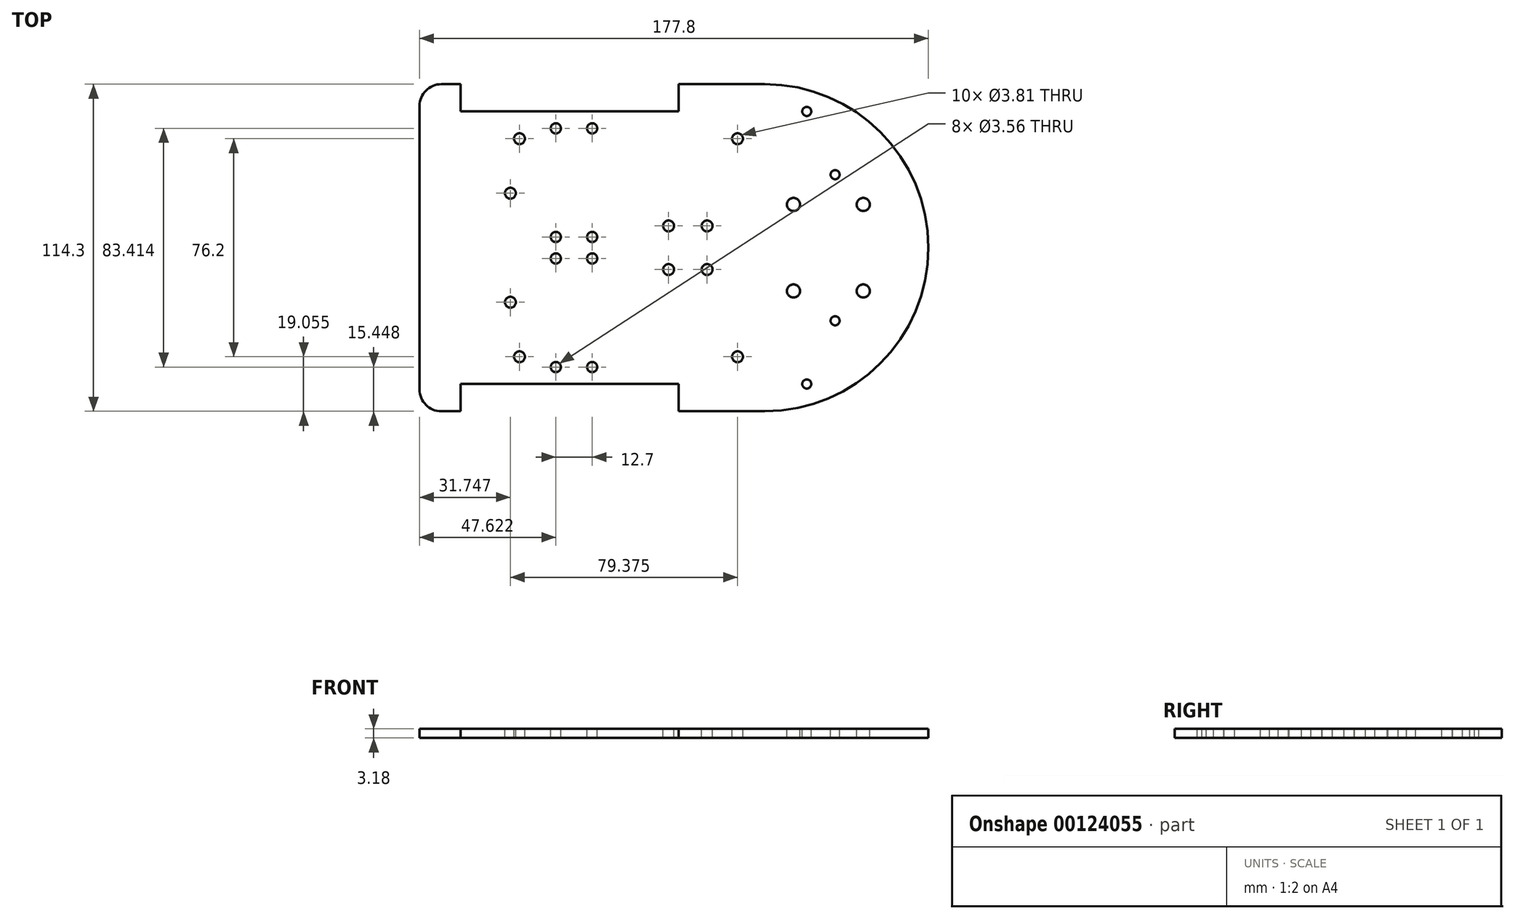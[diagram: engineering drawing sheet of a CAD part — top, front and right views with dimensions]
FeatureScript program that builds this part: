
annotation { "Feature Type Name" : "Feature", "Feature Type Description" : "" }
export const myFeature = defineFeature(function(context is Context, id is Id, definition is map)
    precondition{}
    {
        {
            var Q0;
            Q0=qCreatedBy(makeId("Top.planeOp"),FACE);
            var sketch = newSketch(context, id + "F0", { "sketchPlane" : qUnion([Q0])});
            skLineSegment(sketch, "E0.bottom", {"start": v(-54.24, -6.62) * mm, "end": v(123.56, -6.62) * mm});
            skLineSegment(sketch, "E0.top", {"start": v(-54.24, 107.68) * mm, "end": v(123.56, 107.68) * mm});
            skLineSegment(sketch, "E0.left", {"start": v(-54.24, -6.62) * mm, "end": v(-54.24, 107.68) * mm});
            skLineSegment(sketch, "E0.right", {"start": v(123.56, -6.62) * mm, "end": v(123.56, 107.68) * mm});
            skSolve(sketch);
        }
        {
            var Q0;
            Q0=makeQuery(id+"F0.imprint","IMPRINT",FACE,{"disambiguationData":[TD([[makeQuery(id+"F0.imprint","IMPRINT",EDGE,{"derivedFrom":sQuery(id+"F0.wireOp",EDGE,"E0.bottom")}),1.0]])]});
            extrude(context, id + "F1", {"entities" : qUnion([Q0]), "depth" : 3.17 * mm});
        }
        {
            var Q0;
            Q0=makeQuery(id+"F1.opExtrude","SWEPT_EDGE",EDGE,{"disambiguationData":[OSD([sQuery(id+"F0.wireOp",EDGE,"E0.top"),sQuery(id+"F0.wireOp",EDGE,"E0.left")])]});
            var Q1;
            Q1=makeQuery(id+"F1.opExtrude","SWEPT_EDGE",EDGE,{"disambiguationData":[OSD([sQuery(id+"F0.wireOp",EDGE,"E0.bottom"),sQuery(id+"F0.wireOp",EDGE,"E0.left")])]});
            fillet(context, id + "F2", {"entities" : qUnion([Q0, Q1]), "radius" : 7.62 * mm, "tangentPropagation" : true, "allowEdgeOverflow" : false});
        }
        {
            var Q0;
            Q0=makeQuery(id+"F1.opExtrude","CAP_FACE",FACE,{"disambiguationData":[OSD([sQuery(id+"F0.wireOp",EDGE,"E0.bottom"),sQuery(id+"F0.wireOp",EDGE,"E0.top"),sQuery(id+"F0.wireOp",EDGE,"E0.left"),sQuery(id+"F0.wireOp",EDGE,"E0.right")])],"isStart":false});
            var sketch = newSketch(context, id + "F3", { "sketchPlane" : qUnion([Q0])});
            skLineSegment(sketch, "E1.bottom", {"start": v(-39.96, -6.62) * mm, "end": v(36.24, -6.62) * mm});
            skLineSegment(sketch, "E1.top", {"start": v(-39.96, 2.9) * mm, "end": v(36.24, 2.9) * mm});
            skLineSegment(sketch, "E1.left", {"start": v(-39.96, -6.62) * mm, "end": v(-39.96, 2.9) * mm});
            skLineSegment(sketch, "E1.right", {"start": v(36.24, -6.62) * mm, "end": v(36.24, 2.9) * mm});
            skLineSegment(sketch, "E2.bottom", {"start": v(-39.96, 98.16) * mm, "end": v(36.24, 98.16) * mm});
            skLineSegment(sketch, "E2.top", {"start": v(-39.96, 107.68) * mm, "end": v(36.24, 107.68) * mm});
            skLineSegment(sketch, "E2.left", {"start": v(-39.96, 98.16) * mm, "end": v(-39.96, 107.68) * mm});
            skLineSegment(sketch, "E2.right", {"start": v(36.24, 98.16) * mm, "end": v(36.24, 107.68) * mm});
            skSolve(sketch);
        }
        {
            var Q0;
            Q0=makeQuery(id+"F3.imprint","IMPRINT",FACE,{"disambiguationData":[TD([[makeQuery(id+"F3.imprint","IMPRINT",EDGE,{"derivedFrom":sQuery(id+"F3.wireOp",EDGE,"E1.bottom")}),1.0]])]});
            var Q1;
            Q1=makeQuery(id+"F3.imprint","IMPRINT",FACE,{"disambiguationData":[TD([[makeQuery(id+"F3.imprint","IMPRINT",EDGE,{"derivedFrom":sQuery(id+"F3.wireOp",EDGE,"E2.bottom")}),1.0]])]});
            extrude(context, id + "F4", {"entities" : qUnion([Q0, Q1]), "operationType" : NewBodyOperationType.REMOVE, "oppositeDirection" : true, "depth" : 25.4 * mm});
        }
        {
            var Q0;
            Q0=makeQuery(id+"F1.opExtrude","CAP_FACE",FACE,{"disambiguationData":[OSD([sQuery(id+"F0.wireOp",EDGE,"E0.bottom"),sQuery(id+"F0.wireOp",EDGE,"E0.top"),sQuery(id+"F0.wireOp",EDGE,"E0.left"),sQuery(id+"F0.wireOp",EDGE,"E0.right")])],"isStart":false});
            var sketch = newSketch(context, id + "F5", { "sketchPlane" : qUnion([Q0])});
            skPoint(sketch, "E3", {"position": v(-6.62, 8.83) * mm});
            skPoint(sketch, "E4", {"position": v(-6.62, 46.78) * mm});
            skPoint(sketch, "E5", {"position": v(-6.62, 54.3) * mm});
            skPoint(sketch, "E6", {"position": v(-6.62, 92.24) * mm});
            skPoint(sketch, "E7", {"position": v(6.08, 8.83) * mm});
            skPoint(sketch, "E8", {"position": v(6.08, 46.78) * mm});
            skPoint(sketch, "E9", {"position": v(6.08, 54.3) * mm});
            skPoint(sketch, "E10", {"position": v(6.08, 92.24) * mm});
            skSolve(sketch);
        }
        {
            var Q0;
            Q0=sQuery(id+"F5.wireOp",VERTEX,"E3");
            var Q1;
            Q1=sQuery(id+"F5.wireOp",VERTEX,"E4");
            var Q2;
            Q2=sQuery(id+"F5.wireOp",VERTEX,"E5");
            var Q3;
            Q3=sQuery(id+"F5.wireOp",VERTEX,"E6");
            var Q4;
            Q4=sQuery(id+"F5.wireOp",VERTEX,"E7");
            var Q5;
            Q5=sQuery(id+"F5.wireOp",VERTEX,"E8");
            var Q6;
            Q6=sQuery(id+"F5.wireOp",VERTEX,"E9");
            var Q7;
            Q7=sQuery(id+"F5.wireOp",VERTEX,"E10");
            var Q8;
            Q8=makeQuery(id+"F1.opExtrude","SWEPT_BODY",BODY,{"disambiguationData":[OSD([sQuery(id+"F0.wireOp",EDGE,"E0.bottom"),sQuery(id+"F0.wireOp",EDGE,"E0.top"),sQuery(id+"F0.wireOp",EDGE,"E0.left"),sQuery(id+"F0.wireOp",EDGE,"E0.right")])]});
            hole(context, id + "F6", {"style" : HoleStyle.SIMPLE, "endStyle" : HoleEndStyle.THROUGH, "holeDiameter" : 3.56 * mm, "locations" : qUnion([Q0, Q1, Q2, Q3, Q4, Q5, Q6, Q7]), "scope" : qUnion([Q8]), "isTappedThrough" : true});
        }
        {
            var Q0;
            Q0=makeQuery(id+"F1.opExtrude","CAP_FACE",FACE,{"disambiguationData":[OSD([sQuery(id+"F0.wireOp",EDGE,"E0.bottom"),sQuery(id+"F0.wireOp",EDGE,"E0.top"),sQuery(id+"F0.wireOp",EDGE,"E0.left"),sQuery(id+"F0.wireOp",EDGE,"E0.right")])],"isStart":false});
            var sketch = newSketch(context, id + "F7", { "sketchPlane" : qUnion([Q0])});
            skPoint(sketch, "E11", {"position": v(32.78, 58.15) * mm});
            skPoint(sketch, "E12", {"position": v(32.78, 42.91) * mm});
            skPoint(sketch, "E13", {"position": v(46.24, 42.91) * mm});
            skPoint(sketch, "E14", {"position": v(46.24, 58.15) * mm});
            skSolve(sketch);
        }
        {
            var Q0;
            Q0=sQuery(id+"F7.wireOp",VERTEX,"E12");
            var Q1;
            Q1=sQuery(id+"F7.wireOp",VERTEX,"E13");
            var Q2;
            Q2=sQuery(id+"F7.wireOp",VERTEX,"E14");
            var Q3;
            Q3=sQuery(id+"F7.wireOp",VERTEX,"E11");
            var Q4;
            Q4=makeQuery(id+"F1.opExtrude","SWEPT_BODY",BODY,{"disambiguationData":[OSD([sQuery(id+"F0.wireOp",EDGE,"E0.bottom"),sQuery(id+"F0.wireOp",EDGE,"E0.top"),sQuery(id+"F0.wireOp",EDGE,"E0.left"),sQuery(id+"F0.wireOp",EDGE,"E0.right")])]});
            hole(context, id + "F8", {"style" : HoleStyle.SIMPLE, "endStyle" : HoleEndStyle.THROUGH, "holeDiameter" : 3.8 * mm, "locations" : qUnion([Q0, Q1, Q2, Q3]), "scope" : qUnion([Q4]), "isTappedThrough" : true});
        }
        {
            var Q0;
            Q0=makeQuery(id+"F1.opExtrude","CAP_FACE",FACE,{"disambiguationData":[OSD([sQuery(id+"F0.wireOp",EDGE,"E0.bottom"),sQuery(id+"F0.wireOp",EDGE,"E0.top"),sQuery(id+"F0.wireOp",EDGE,"E0.left"),sQuery(id+"F0.wireOp",EDGE,"E0.right")])],"isStart":false});
            var sketch = newSketch(context, id + "F9", { "sketchPlane" : qUnion([Q0])});
            skPoint(sketch, "E15", {"position": v(46.85, 26.53) * mm});
            skPoint(sketch, "E16", {"position": v(46.85, 74.54) * mm});
            skPoint(sketch, "E17", {"position": v(97.62, 59.68) * mm});
            skPoint(sketch, "E18", {"position": v(97.62, 31.74) * mm});
            skSolve(sketch);
        }
        {
            var Q0;
            Q0=makeQuery(id+"F1.opExtrude","CAP_FACE",FACE,{"disambiguationData":[OSD([sQuery(id+"F0.wireOp",EDGE,"E0.bottom"),sQuery(id+"F0.wireOp",EDGE,"E0.top"),sQuery(id+"F0.wireOp",EDGE,"E0.left"),sQuery(id+"F0.wireOp",EDGE,"E0.right")])],"isStart":false});
            var sketch = newSketch(context, id + "F10", { "sketchPlane" : qUnion([Q0])});
            skPoint(sketch, "E19", {"position": v(-22.5, 69.58) * mm});
            skPoint(sketch, "E20", {"position": v(-22.5, 31.48) * mm});
            skSolve(sketch);
        }
        {
            var Q0;
            Q0=sQuery(id+"F10.wireOp",VERTEX,"E20");
            var Q1;
            Q1=sQuery(id+"F10.wireOp",VERTEX,"E19");
            var Q2;
            Q2=makeQuery(id+"F1.opExtrude","SWEPT_BODY",BODY,{"disambiguationData":[OSD([sQuery(id+"F0.wireOp",EDGE,"E0.bottom"),sQuery(id+"F0.wireOp",EDGE,"E0.top"),sQuery(id+"F0.wireOp",EDGE,"E0.left"),sQuery(id+"F0.wireOp",EDGE,"E0.right")])]});
            hole(context, id + "F11", {"style" : HoleStyle.SIMPLE, "endStyle" : HoleEndStyle.THROUGH, "holeDiameter" : 3.8 * mm, "locations" : qUnion([Q0, Q1]), "scope" : qUnion([Q2]), "isTappedThrough" : true});
        }
        {
            var Q0;
            Q0=makeQuery(id+"F1.opExtrude","CAP_FACE",FACE,{"disambiguationData":[OSD([sQuery(id+"F0.wireOp",EDGE,"E0.bottom"),sQuery(id+"F0.wireOp",EDGE,"E0.top"),sQuery(id+"F0.wireOp",EDGE,"E0.left"),sQuery(id+"F0.wireOp",EDGE,"E0.right")])],"isStart":false});
            var sketch = newSketch(context, id + "F12", { "sketchPlane" : qUnion([Q0])});
            skPoint(sketch, "E21", {"position": v(76.44, 35.42) * mm});
            skPoint(sketch, "E22", {"position": v(76.44, 65.65) * mm});
            skPoint(sketch, "E23", {"position": v(100.82, 35.42) * mm});
            skPoint(sketch, "E24", {"position": v(100.82, 65.65) * mm});
            skSolve(sketch);
        }
        {
            var Q0;
            Q0=sQuery(id+"F12.wireOp",VERTEX,"E22");
            var Q1;
            Q1=sQuery(id+"F12.wireOp",VERTEX,"E21");
            var Q2;
            Q2=sQuery(id+"F12.wireOp",VERTEX,"E23");
            var Q3;
            Q3=sQuery(id+"F12.wireOp",VERTEX,"E24");
            var Q4;
            Q4=makeQuery(id+"F1.opExtrude","SWEPT_BODY",BODY,{"disambiguationData":[OSD([sQuery(id+"F0.wireOp",EDGE,"E0.bottom"),sQuery(id+"F0.wireOp",EDGE,"E0.top"),sQuery(id+"F0.wireOp",EDGE,"E0.left"),sQuery(id+"F0.wireOp",EDGE,"E0.right")])]});
            hole(context, id + "F13", {"style" : HoleStyle.SIMPLE, "endStyle" : HoleEndStyle.THROUGH, "holeDiameter" : 4.57 * mm, "locations" : qUnion([Q0, Q1, Q2, Q3]), "scope" : qUnion([Q4]), "isTappedThrough" : true});
        }
        {
            var Q0;
            Q0=makeQuery(id+"F1.opExtrude","CAP_FACE",FACE,{"disambiguationData":[OSD([sQuery(id+"F0.wireOp",EDGE,"E0.bottom"),sQuery(id+"F0.wireOp",EDGE,"E0.top"),sQuery(id+"F0.wireOp",EDGE,"E0.left"),sQuery(id+"F0.wireOp",EDGE,"E0.right")])],"isStart":false});
            var sketch = newSketch(context, id + "F14", { "sketchPlane" : qUnion([Q0])});
            skPoint(sketch, "E25", {"position": v(-19.32, 12.43) * mm});
            skPoint(sketch, "E26", {"position": v(-19.32, 88.63) * mm});
            skPoint(sketch, "E27", {"position": v(56.88, 88.63) * mm});
            skPoint(sketch, "E28", {"position": v(56.88, 12.43) * mm});
            skSolve(sketch);
        }
        {
            var Q0;
            Q0=sQuery(id+"F14.wireOp",VERTEX,"E25");
            var Q1;
            Q1=sQuery(id+"F14.wireOp",VERTEX,"E26");
            var Q2;
            Q2=sQuery(id+"F14.wireOp",VERTEX,"E27");
            var Q3;
            Q3=sQuery(id+"F14.wireOp",VERTEX,"E28");
            var Q4;
            Q4=makeQuery(id+"F1.opExtrude","SWEPT_BODY",BODY,{"disambiguationData":[OSD([sQuery(id+"F0.wireOp",EDGE,"E0.bottom"),sQuery(id+"F0.wireOp",EDGE,"E0.top"),sQuery(id+"F0.wireOp",EDGE,"E0.left"),sQuery(id+"F0.wireOp",EDGE,"E0.right")])]});
            hole(context, id + "F15", {"style" : HoleStyle.SIMPLE, "endStyle" : HoleEndStyle.THROUGH, "holeDiameter" : 3.8 * mm, "locations" : qUnion([Q0, Q1, Q2, Q3]), "scope" : qUnion([Q4]), "isTappedThrough" : true});
        }
        {
            var Q0;
            Q0=makeQuery(id+"F1.opExtrude","SWEPT_EDGE",EDGE,{"disambiguationData":[OSD([sQuery(id+"F0.wireOp",EDGE,"E0.bottom"),sQuery(id+"F0.wireOp",EDGE,"E0.right")])]});
            var Q1;
            Q1=makeQuery(id+"F1.opExtrude","SWEPT_EDGE",EDGE,{"disambiguationData":[OSD([sQuery(id+"F0.wireOp",EDGE,"E0.top"),sQuery(id+"F0.wireOp",EDGE,"E0.right")])]});
            fillet(context, id + "F16", {"entities" : qUnion([Q0, Q1]), "radius" : 57.15 * mm, "tangentPropagation" : true, "allowEdgeOverflow" : false});
        }
        {
            var Q0;
            {var subQ0=sQuery(id+"F0.wireOp",EDGE,"E0.right");Q0=makeQuery(id+"F9.imprint","IMPRINT",FACE,{"disambiguationData":[TD([[makeQuery(id+"F9.imprint","IMPRINT",EDGE,{"derivedFrom":makeQuery(id+"F1.opExtrude","CAP_EDGE",EDGE,{"disambiguationData":[OSD([subQ0])],"isStart":false})}),1.0]])]});}
            var sketch = newSketch(context, id + "F17", { "sketchPlane" : qUnion([Q0])});
            skPoint(sketch, "E29", {"position": v(81.08, 2.9) * mm});
            skPoint(sketch, "E30", {"position": v(90.98, 25) * mm});
            skPoint(sketch, "E31", {"position": v(90.98, 76.06) * mm});
            skPoint(sketch, "E32", {"position": v(81.08, 98.16) * mm});
            skLineSegment(sketch, "E33", {"start": v(90.91, 36.78) * mm, "end": v(90.91, 11.6) * mm});
            skLineSegment(sketch, "E34", {"start": v(81.08, 2.9) * mm, "end": v(81.08, 24.91) * mm});
            skSolve(sketch);
        }
        {
            var Q0;
            Q0=sQuery(id+"F17.wireOp",VERTEX,"E29");
            var Q1;
            Q1=sQuery(id+"F17.wireOp",VERTEX,"E30");
            var Q2;
            Q2=sQuery(id+"F17.wireOp",VERTEX,"E31");
            var Q3;
            Q3=sQuery(id+"F17.wireOp",VERTEX,"E32");
            var Q4;
            Q4=makeQuery(id+"F1.opExtrude","SWEPT_BODY",BODY,{"disambiguationData":[OSD([sQuery(id+"F0.wireOp",EDGE,"E0.bottom"),sQuery(id+"F0.wireOp",EDGE,"E0.top"),sQuery(id+"F0.wireOp",EDGE,"E0.left"),sQuery(id+"F0.wireOp",EDGE,"E0.right")])]});
            hole(context, id + "F18", {"style" : HoleStyle.SIMPLE, "endStyle" : HoleEndStyle.THROUGH, "holeDiameter" : 3.17 * mm, "locations" : qUnion([Q0, Q1, Q2, Q3]), "scope" : qUnion([Q4]), "isTappedThrough" : true});
        }
    });
